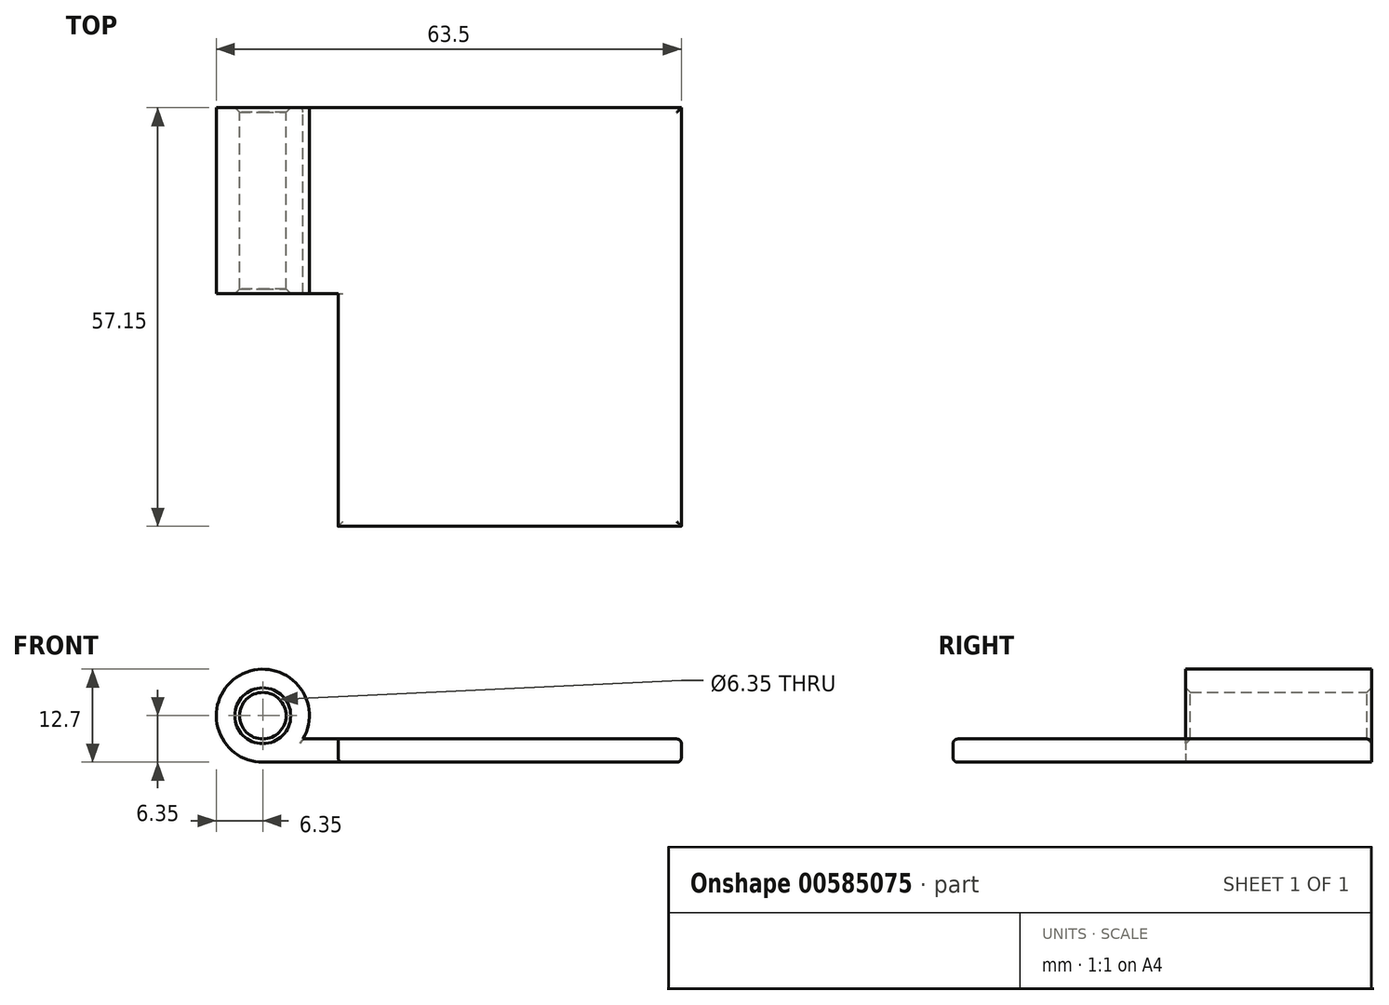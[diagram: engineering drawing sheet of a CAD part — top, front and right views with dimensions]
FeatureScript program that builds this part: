
annotation { "Feature Type Name" : "Feature", "Feature Type Description" : "" }
export const myFeature = defineFeature(function(context is Context, id is Id, definition is map)
    precondition{}
    {
        {
            var Q0;
            Q0=qCreatedBy(makeId("Front.planeOp"),FACE);
            var sketch = newSketch(context, id + "F0", { "sketchPlane" : qUnion([Q0])});
            skCircle(sketch, "E0", {"center": v(0, 0) * mm, "radius": 3.18 * mm});
            skLineSegment(sketch, "E1.top", {"start": v(0, -6.35) * mm, "end": v(57.15, -6.35) * mm});
            skLineSegment(sketch, "E1.right", {"start": v(57.15, -3.18) * mm, "end": v(57.15, -6.35) * mm});
            skLineSegment(sketch, "E2", {"start": v(57.15, -3.18) * mm, "end": v(5.5, -3.18) * mm});
            skArc(sketch, "E3", {"start": v(5.5, -3.18) * mm, "mid": v(-3.18, 5.5) * mm, "end": v(0, -6.35) * mm});
            skLineSegment(sketch, "E4", {"start": v(10.27, -3.18) * mm, "end": v(10.27, -6.35) * mm});
            skSolve(sketch);
        }
        {
            var Q0;
            Q0=makeQuery(id+"F0.imprint","IMPRINT",FACE,{"disambiguationData":[TD([[makeQuery(id+"F0.imprint","IMPRINT",EDGE,{"derivedFrom":sQuery(id+"F0.wireOp",EDGE,"E0")}),-1.0]])]});
            extrude(context, id + "F1", {"entities" : qUnion([Q0]), "depth" : 25.4 * mm, "offsetDistance" : 25.4 * mm});
        }
        {
            var Q0;
            {var subQ0=sQuery(id+"F0.wireOp",EDGE,"E1.right");Q0=makeQuery(id+"F0.imprint","IMPRINT",FACE,{"disambiguationData":[TD([[makeQuery(id+"F0.imprint","IMPRINT",EDGE,{"derivedFrom":subQ0}),-1.0]])]});}
            extrude(context, id + "F2", {"entities" : qUnion([Q0]), "operationType" : NewBodyOperationType.ADD, "depth" : 57.15 * mm, "offsetDistance" : 25.4 * mm});
        }
        {
            var Q0;
            Q0=makeQuery(id+"F2.opExtrude","CAP_EDGE",EDGE,{"disambiguationData":[OSD([sQuery(id+"F0.wireOp",EDGE,"E2")])],"isStart":false});
            var Q1;
            Q1=makeQuery(id+"F2.opExtrude","CAP_EDGE",EDGE,{"disambiguationData":[OSD([sQuery(id+"F0.wireOp",EDGE,"E1.top")])],"isStart":false});
            var Q2;
            Q2=makeQuery(id+"F2.opExtrude","SWEPT_EDGE",EDGE,{"disambiguationData":[OSD([sQuery(id+"F0.wireOp",EDGE,"E1.right"),sQuery(id+"F0.wireOp",EDGE,"E2")])]});
            var Q3;
            Q3=makeQuery(id+"F2.opExtrude","SWEPT_EDGE",EDGE,{"disambiguationData":[OSD([sQuery(id+"F0.wireOp",EDGE,"E1.top"),sQuery(id+"F0.wireOp",EDGE,"E1.right")])]});
            var Q4;
            Q4=makeQuery(id+"F2.opExtrude","CAP_EDGE",EDGE,{"disambiguationData":[OSD([sQuery(id+"F0.wireOp",EDGE,"E2")])],"isStart":true});
            var Q5;
            {var subQ0=sQuery(id+"F0.wireOp",EDGE,"fWPBAXFR-IpgK-OF10-LHZP-lVou9CoigAbk");var subQ1=sQuery(id+"F0.wireOp",EDGE,"E3");var subQ2=sQuery(id+"F0.wireOp",EDGE,"E2");Q5=makeQuery(id+"F2.boolean.opBoolean","MERGE",EDGE,{"derivedFrom":[makeQuery(id+"F1.opExtrude","SWEPT_EDGE",EDGE,{"disambiguationData":[OSD([subQ2,subQ1,subQ0])]}),makeQuery(id+"F2.opExtrude","SWEPT_EDGE",EDGE,{"disambiguationData":[OSD([subQ2,subQ1,subQ0])]})]});}
            var Q6;
            Q6=makeQuery(id+"F2.opExtrude","SWEPT_EDGE",EDGE,{"disambiguationData":[OSD([sQuery(id+"F0.wireOp",EDGE,"E1.top"),sQuery(id+"F0.wireOp",EDGE,"fWPBAXFR-IpgK-OF10-LHZP-lVou9CoigAbk")])]});
            fillet(context, id + "F3", {"entities" : qUnion([Q0, Q1, Q2, Q3, Q4, Q5, Q6]), "radius" : 0.64 * mm, "tangentPropagation" : true, "allowEdgeOverflow" : false});
        }
        {
            var Q0;
            Q0=makeQuery(id+"F1.opExtrude","CAP_EDGE",EDGE,{"disambiguationData":[OSD([sQuery(id+"F0.wireOp",EDGE,"E0")])],"isStart":false});
            var Q1;
            Q1=makeQuery(id+"F1.opExtrude","CAP_EDGE",EDGE,{"disambiguationData":[OSD([sQuery(id+"F0.wireOp",EDGE,"E0")])],"isStart":true});
            chamfer(context, id + "F4", {"entities" : qUnion([Q0, Q1]), "width" : 0.64 * mm, "tangentPropagation" : true});
        }
    });
